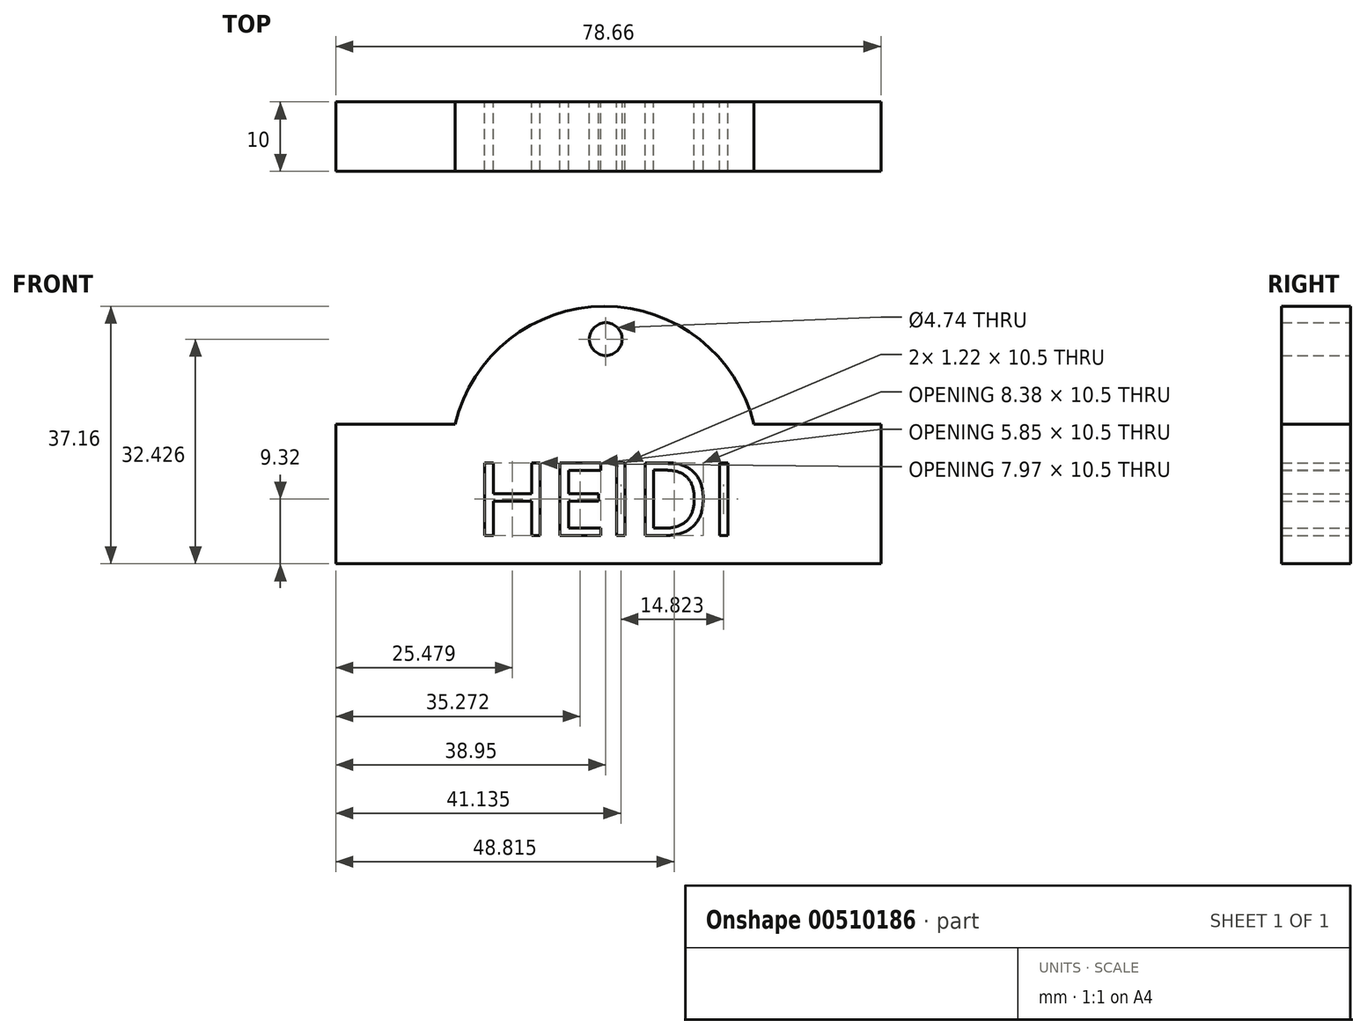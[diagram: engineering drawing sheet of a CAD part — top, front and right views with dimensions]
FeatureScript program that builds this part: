
annotation { "Feature Type Name" : "Feature", "Feature Type Description" : "" }
export const myFeature = defineFeature(function(context is Context, id is Id, definition is map)
    precondition{}
    {
        {
            var Q0;
            Q0=qCreatedBy(makeId("Front.planeOp"),FACE);
            var sketch = newSketch(context, id + "F0", { "sketchPlane" : qUnion([Q0])});
            skLineSegment(sketch, "E0.bottom", {"start": v(-38.95, 0) * mm, "end": v(39.7, 0) * mm});
            skLineSegment(sketch, "E0.top", {"start": v(-38.95, 20.14) * mm, "end": v(39.7, 20.14) * mm});
            skLineSegment(sketch, "E0.left", {"start": v(-38.95, 0) * mm, "end": v(-38.95, 20.14) * mm});
            skLineSegment(sketch, "E0.right", {"start": v(39.7, 0) * mm, "end": v(39.7, 20.14) * mm});
            skArc(sketch, "E1", {"start": v(21.37, 20.14) * mm, "mid": v(-0.19, 37.16) * mm, "end": v(-21.74, 20.14) * mm});
            skCircle(sketch, "E2", {"center": v(0, 32.43) * mm, "radius": 2.37 * mm});
            skText(sketch, "E3", { "text": "HEIDI", "fontName": "OpenSans-Regular.ttf"});
            const initialGuessF0  = {"E3": [-0.0189, 0.00407, 1, 0, 0.01059]};
            skSetInitialGuess(sketch, initialGuessF0);
            skSolve(sketch);
        }
        {
            var Q0;
            Q0=makeQuery(id+"F0.imprint","IMPRINT",FACE,{"disambiguationData":[TD([[makeQuery(id+"F0.imprint","IMPRINT",EDGE,{"derivedFrom":sQuery(id+"F0.wireOp",EDGE,"E0.bottom")}),1.0]])]});
            var Q1;
            {var subQ0=sQuery(id+"F0.wireOp",EDGE,"E1");Q1=makeQuery(id+"F0.imprint","IMPRINT",FACE,{"disambiguationData":[TD([[makeQuery(id+"F0.imprint","IMPRINT",EDGE,{"derivedFrom":subQ0}),1.0]])]});}
            var Q2;
            Q2=makeQuery(id+"F0.imprint","IMPRINT",FACE,{"disambiguationData":[TD([[makeQuery(id+"F0.imprint","IMPRINT",EDGE,{"derivedFrom":sQuery(id+"F0.wireOp",EDGE,"E3.sketch_text.stroke-35")}),1.0]])]});
            extrude(context, id + "F1", {"entities" : qUnion([Q0, Q1, Q2]), "depth" : 10 * mm});
        }
    });
